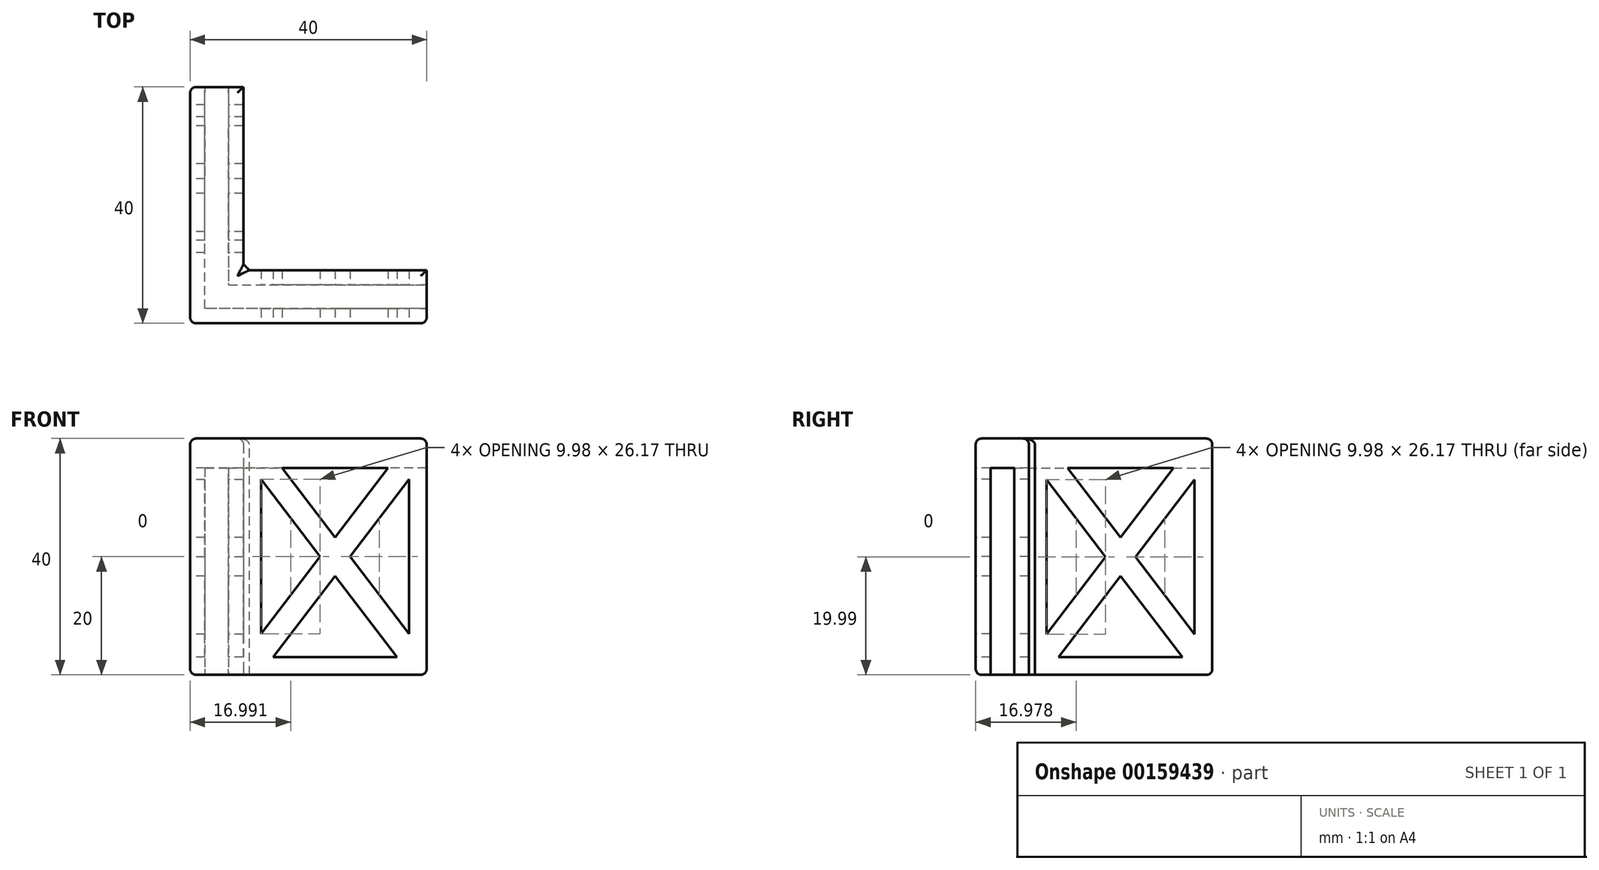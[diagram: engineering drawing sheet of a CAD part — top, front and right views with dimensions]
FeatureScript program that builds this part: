
annotation { "Feature Type Name" : "Feature", "Feature Type Description" : "" }
export const myFeature = defineFeature(function(context is Context, id is Id, definition is map)
    precondition{}
    {
        {
            var Q0;
            Q0=qCreatedBy(makeId("Top.planeOp"),FACE);
            var sketch = newSketch(context, id + "F0", { "sketchPlane" : qUnion([Q0])});
            skLineSegment(sketch, "E0.bottom", {"start": v(-0.94, -7.53) * mm, "end": v(39.06, -7.53) * mm});
            skLineSegment(sketch, "E0.top", {"start": v(-0.94, -47.53) * mm, "end": v(39.06, -47.53) * mm});
            skLineSegment(sketch, "E0.left", {"start": v(-0.94, -7.53) * mm, "end": v(-0.94, -47.53) * mm});
            skLineSegment(sketch, "E0.right", {"start": v(39.06, -7.53) * mm, "end": v(39.06, -47.53) * mm});
            skSolve(sketch);
        }
        {
            var Q0;
            Q0=makeQuery(id+"F0.imprint","IMPRINT",FACE,{"disambiguationData":[TD([[makeQuery(id+"F0.imprint","IMPRINT",EDGE,{"derivedFrom":sQuery(id+"F0.wireOp",EDGE,"E0.bottom")}),-1.0]])]});
            extrude(context, id + "F1", {"entities" : qUnion([Q0]), "depth" : 40 * mm});
        }
        {
            var Q0;
            Q0=makeQuery(id+"F1.opExtrude","CAP_FACE",FACE,{"disambiguationData":[OSD([sQuery(id+"F0.wireOp",EDGE,"E0.bottom"),sQuery(id+"F0.wireOp",EDGE,"E0.top"),sQuery(id+"F0.wireOp",EDGE,"E0.left"),sQuery(id+"F0.wireOp",EDGE,"E0.right")])],"isStart":true});
            var sketch = newSketch(context, id + "F2", { "sketchPlane" : qUnion([Q0])});
            skLineSegment(sketch, "E1", {"start": v(39.06, 45.03) * mm, "end": v(1.56, 45.03) * mm});
            skLineSegment(sketch, "E2", {"start": v(1.56, 45.03) * mm, "end": v(1.56, 7.53) * mm});
            skLineSegment(sketch, "E3", {"start": v(5.56, 7.53) * mm, "end": v(5.56, 41.03) * mm});
            skLineSegment(sketch, "E4", {"start": v(5.56, 41.03) * mm, "end": v(39.06, 41.03) * mm});
            skLineSegment(sketch, "E5", {"start": v(39.06, 38.53) * mm, "end": v(8.06, 38.53) * mm});
            skLineSegment(sketch, "E6", {"start": v(8.06, 38.53) * mm, "end": v(8.06, 7.53) * mm});
            skSolve(sketch);
        }
        {
            var Q0;
            {var subQ3=sQuery(id+"F2.wireOp",EDGE,"E1");Q0=makeQuery(id+"F2.imprint","IMPRINT",FACE,{"disambiguationData":[TD([[makeQuery(id+"F2.imprint","IMPRINT",EDGE,{"derivedFrom":subQ3}),1.0]])]});}
            extrude(context, id + "F3", {"entities" : qUnion([Q0]), "operationType" : NewBodyOperationType.REMOVE, "oppositeDirection" : true, "depth" : 35 * mm});
        }
        {
            var Q0;
            {var subQ0=sQuery(id+"F2.wireOp",EDGE,"E5");Q0=makeQuery(id+"F2.imprint","IMPRINT",FACE,{"disambiguationData":[TD([[makeQuery(id+"F2.imprint","IMPRINT",EDGE,{"derivedFrom":subQ0}),1.0]])]});}
            extrude(context, id + "F4", {"entities" : qUnion([Q0]), "operationType" : NewBodyOperationType.REMOVE, "endBound" : BoundingType.THROUGH_ALL, "oppositeDirection" : true, "depth" : 25 * mm});
        }
        {
            var Q0;
            Q0=makeQuery(id+"F4.boolean.opBoolean","COPY",EDGE,{"derivedFrom":makeQuery(id+"F4.opExtrude","SWEPT_EDGE",EDGE,{"disambiguationData":[OSD([sQuery(id+"F0.wireOp",EDGE,"E0.bottom"),sQuery(id+"F2.wireOp",EDGE,"E6")])]})});
            var Q1;
            Q1=makeQuery(id+"F1.opExtrude","SWEPT_EDGE",EDGE,{"disambiguationData":[OSD([sQuery(id+"F0.wireOp",EDGE,"E0.bottom"),sQuery(id+"F0.wireOp",EDGE,"E0.left")])]});
            var Q2;
            Q2=makeQuery(id+"F1.opExtrude","SWEPT_EDGE",EDGE,{"disambiguationData":[OSD([sQuery(id+"F0.wireOp",EDGE,"E0.top"),sQuery(id+"F0.wireOp",EDGE,"E0.left")])]});
            var Q3;
            Q3=makeQuery(id+"F4.boolean.opBoolean","COPY",EDGE,{"derivedFrom":makeQuery(id+"F4.opExtrude","SWEPT_EDGE",EDGE,{"disambiguationData":[OSD([sQuery(id+"F0.wireOp",EDGE,"E0.right"),sQuery(id+"F2.wireOp",EDGE,"E5")])]})});
            var Q4;
            Q4=makeQuery(id+"F1.opExtrude","SWEPT_EDGE",EDGE,{"disambiguationData":[OSD([sQuery(id+"F0.wireOp",EDGE,"E0.top"),sQuery(id+"F0.wireOp",EDGE,"E0.right")])]});
            var Q5;
            Q5=makeQuery(id+"F1.opExtrude","CAP_EDGE",EDGE,{"disambiguationData":[OSD([sQuery(id+"F0.wireOp",EDGE,"E0.right")])],"isStart":false});
            var Q6;
            Q6=makeQuery(id+"F1.opExtrude","CAP_EDGE",EDGE,{"disambiguationData":[OSD([sQuery(id+"F0.wireOp",EDGE,"E0.top")])],"isStart":false});
            var Q7;
            Q7=makeQuery(id+"F4.boolean.opBoolean","INTERSECT",EDGE,{"derivedFrom":[makeQuery(id+"F1.opExtrude","CAP_FACE",FACE,{"disambiguationData":[OSD([sQuery(id+"F0.wireOp",EDGE,"E0.bottom"),sQuery(id+"F0.wireOp",EDGE,"E0.top"),sQuery(id+"F0.wireOp",EDGE,"E0.left"),sQuery(id+"F0.wireOp",EDGE,"E0.right")])],"isStart":false}),makeQuery(id+"F4.opExtrude","SWEPT_FACE",FACE,{"disambiguationData":[OSD([sQuery(id+"F2.wireOp",EDGE,"E5")])]})]});
            var Q8;
            Q8=makeQuery(id+"F4.boolean.opBoolean","INTERSECT",EDGE,{"derivedFrom":[makeQuery(id+"F1.opExtrude","CAP_FACE",FACE,{"disambiguationData":[OSD([sQuery(id+"F0.wireOp",EDGE,"E0.bottom"),sQuery(id+"F0.wireOp",EDGE,"E0.top"),sQuery(id+"F0.wireOp",EDGE,"E0.left"),sQuery(id+"F0.wireOp",EDGE,"E0.right")])],"isStart":false}),makeQuery(id+"F4.opExtrude","SWEPT_FACE",FACE,{"disambiguationData":[OSD([sQuery(id+"F2.wireOp",EDGE,"E6")])]})]});
            var Q9;
            Q9=makeQuery(id+"F1.opExtrude","CAP_EDGE",EDGE,{"disambiguationData":[OSD([sQuery(id+"F0.wireOp",EDGE,"E0.bottom")])],"isStart":false});
            var Q10;
            Q10=makeQuery(id+"F1.opExtrude","CAP_EDGE",EDGE,{"disambiguationData":[OSD([sQuery(id+"F0.wireOp",EDGE,"E0.left")])],"isStart":false});
            var Q11;
            Q11=makeQuery(id+"F1.opExtrude","CAP_EDGE",EDGE,{"disambiguationData":[OSD([sQuery(id+"F0.wireOp",EDGE,"E0.top")])],"isStart":true});
            var Q12;
            Q12=makeQuery(id+"F4.boolean.opBoolean","COPY",EDGE,{"derivedFrom":makeQuery(id+"F4.opExtrude","CAP_EDGE",EDGE,{"disambiguationData":[OSD([sQuery(id+"F2.wireOp",EDGE,"E5")])],"isStart":true})});
            var Q13;
            Q13=makeQuery(id+"F4.boolean.opBoolean","COPY",EDGE,{"derivedFrom":makeQuery(id+"F4.opExtrude","CAP_EDGE",EDGE,{"disambiguationData":[OSD([sQuery(id+"F2.wireOp",EDGE,"E6")])],"isStart":true})});
            var Q14;
            Q14=makeQuery(id+"F1.opExtrude","CAP_EDGE",EDGE,{"disambiguationData":[OSD([sQuery(id+"F0.wireOp",EDGE,"E0.left")])],"isStart":true});
            var Q15;
            {var subQ0=sQuery(id+"F0.wireOp",EDGE,"E0.right");var subQ1=sQuery(id+"F0.wireOp",EDGE,"E0.top");Q15=makeQuery(id+"F3.boolean.opBoolean","SPLIT",EDGE,{"disambiguationData":[TD([makeQuery(id+"F1.opExtrude","SWEPT_FACE",FACE,{"disambiguationData":[OSD([subQ1])]})])],"derivedFrom":makeQuery(id+"F1.opExtrude","CAP_EDGE",EDGE,{"disambiguationData":[OSD([subQ0])],"isStart":true})});}
            var Q16;
            {var subQ0=sQuery(id+"F0.wireOp",EDGE,"E0.bottom");var subQ1=sQuery(id+"F0.wireOp",EDGE,"E0.right");Q16=makeQuery(id+"F3.boolean.opBoolean","SPLIT",EDGE,{"disambiguationData":[TD([makeQuery(id+"F1.opExtrude","SWEPT_FACE",FACE,{"disambiguationData":[OSD([subQ0])]})])],"derivedFrom":makeQuery(id+"F1.opExtrude","CAP_EDGE",EDGE,{"disambiguationData":[OSD([subQ1])],"isStart":true})});}
            var Q17;
            {var subQ0=sQuery(id+"F0.wireOp",EDGE,"E0.bottom");var subQ1=sQuery(id+"F0.wireOp",EDGE,"E0.right");Q17=makeQuery(id+"F3.boolean.opBoolean","SPLIT",EDGE,{"disambiguationData":[TD([makeQuery(id+"F1.opExtrude","SWEPT_FACE",FACE,{"disambiguationData":[OSD([subQ1])]})])],"derivedFrom":makeQuery(id+"F1.opExtrude","CAP_EDGE",EDGE,{"disambiguationData":[OSD([subQ0])],"isStart":true})});}
            var Q18;
            {var subQ0=sQuery(id+"F0.wireOp",EDGE,"E0.bottom");var subQ1=sQuery(id+"F0.wireOp",EDGE,"E0.left");Q18=makeQuery(id+"F3.boolean.opBoolean","SPLIT",EDGE,{"disambiguationData":[TD([makeQuery(id+"F1.opExtrude","SWEPT_FACE",FACE,{"disambiguationData":[OSD([subQ1])]})])],"derivedFrom":makeQuery(id+"F1.opExtrude","CAP_EDGE",EDGE,{"disambiguationData":[OSD([subQ0])],"isStart":true})});}
            fillet(context, id + "F5", {"entities" : qUnion([Q0, Q1, Q2, Q3, Q4, Q5, Q6, Q7, Q8, Q9, Q10, Q11, Q12, Q13, Q14, Q15, Q16, Q17, Q18]), "radius" : 1 * mm, "tangentPropagation" : true, "allowEdgeOverflow" : false});
        }
        {
            var Q0;
            Q0=makeQuery(id+"F4.boolean.opBoolean","COPY",EDGE,{"derivedFrom":makeQuery(id+"F4.opExtrude","SWEPT_EDGE",EDGE,{"disambiguationData":[OSD([sQuery(id+"F2.wireOp",EDGE,"E5"),sQuery(id+"F2.wireOp",EDGE,"E6")])]})});
            chamfer(context, id + "F6", {"entities" : qUnion([Q0]), "width" : 1 * mm, "tangentPropagation" : true});
        }
        {
            var Q0;
            Q0=makeQuery(id+"F1.opExtrude","SWEPT_FACE",FACE,{"disambiguationData":[OSD([sQuery(id+"F0.wireOp",EDGE,"E0.top")])]});
            var sketch = newSketch(context, id + "F7", { "sketchPlane" : qUnion([Q0])});
            skLineSegment(sketch, "E7", {"start": v(9.06, 39) * mm, "end": v(9.06, 1) * mm});
            skLineSegment(sketch, "E8", {"start": v(11.57, 39) * mm, "end": v(38.06, 4.3) * mm});
            skLineSegment(sketch, "E9", {"start": v(9.06, 35.7) * mm, "end": v(35.54, 1) * mm});
            skLineSegment(sketch, "E10", {"start": v(35.54, 1) * mm, "end": v(35.3, 0.76) * mm});
            skLineSegment(sketch, "E11", {"start": v(35.54, 39) * mm, "end": v(9.06, 4.3) * mm});
            skLineSegment(sketch, "E12", {"start": v(11.57, 1) * mm, "end": v(38.06, 35.7) * mm});
            skLineSegment(sketch, "E13", {"start": v(14.63, 35) * mm, "end": v(32.5, 35) * mm});
            skLineSegment(sketch, "E14", {"start": v(36.06, 33.08) * mm, "end": v(36.06, 6.92) * mm});
            skLineSegment(sketch, "E15", {"start": v(11.06, 33.08) * mm, "end": v(11.06, 6.92) * mm});
            skLineSegment(sketch, "E16", {"start": v(13.1, 3) * mm, "end": v(34.02, 3) * mm});
            skSolve(sketch);
        }
        {
            var Q0;
            {var subQ0=sQuery(id+"F7.wireOp",EDGE,"E13");Q0=makeQuery(id+"F7.imprint","IMPRINT",FACE,{"disambiguationData":[TD([[makeQuery(id+"F7.imprint","IMPRINT",EDGE,{"derivedFrom":subQ0}),-1.0]])]});}
            var Q1;
            {var subQ0=sQuery(id+"F7.wireOp",EDGE,"E15");Q1=makeQuery(id+"F7.imprint","IMPRINT",FACE,{"disambiguationData":[TD([[makeQuery(id+"F7.imprint","IMPRINT",EDGE,{"derivedFrom":subQ0}),1.0]])]});}
            var Q2;
            {var subQ0=sQuery(id+"F7.wireOp",EDGE,"E16");Q2=makeQuery(id+"F7.imprint","IMPRINT",FACE,{"disambiguationData":[TD([[makeQuery(id+"F7.imprint","IMPRINT",EDGE,{"derivedFrom":subQ0}),1.0]])]});}
            var Q3;
            {var subQ0=sQuery(id+"F7.wireOp",EDGE,"E14");Q3=makeQuery(id+"F7.imprint","IMPRINT",FACE,{"disambiguationData":[TD([[makeQuery(id+"F7.imprint","IMPRINT",EDGE,{"derivedFrom":subQ0}),-1.0]])]});}
            extrude(context, id + "F8", {"entities" : qUnion([Q0, Q1, Q2, Q3]), "operationType" : NewBodyOperationType.REMOVE, "endBound" : BoundingType.THROUGH_ALL, "oppositeDirection" : true, "depth" : 25 * mm});
        }
        {
            var Q0;
            Q0=makeQuery(id+"F1.opExtrude","SWEPT_FACE",FACE,{"disambiguationData":[OSD([sQuery(id+"F0.wireOp",EDGE,"E0.left")])]});
            var sketch = newSketch(context, id + "F9", { "sketchPlane" : qUnion([Q0])});
            skLineSegment(sketch, "E17", {"start": v(37.54, 39) * mm, "end": v(37.54, 1) * mm});
            skLineSegment(sketch, "E18.MirrorCS", {"start": v(35.54, 33.07) * mm, "end": v(35.54, 6.9) * mm});
            skLineSegment(sketch, "E19.MirrorCS", {"start": v(37.54, 35.7) * mm, "end": v(11.06, 1) * mm});
            skLineSegment(sketch, "E20.MirrorCS", {"start": v(35.03, 39) * mm, "end": v(8.54, 4.29) * mm});
            skLineSegment(sketch, "E21.MirrorCS", {"start": v(31.98, 35) * mm, "end": v(14.1, 35) * mm});
            skLineSegment(sketch, "E22.MirrorCS", {"start": v(11.06, 39) * mm, "end": v(37.54, 4.29) * mm});
            skLineSegment(sketch, "E23.MirrorCS", {"start": v(35.03, 1) * mm, "end": v(8.54, 35.7) * mm});
            skLineSegment(sketch, "E24.MirrorCS", {"start": v(10.54, 33.07) * mm, "end": v(10.54, 6.9) * mm});
            skLineSegment(sketch, "E25.MirrorCS", {"start": v(33.5, 3) * mm, "end": v(12.59, 3) * mm});
            skSolve(sketch);
        }
        {
            var Q0;
            {var subQ0=sQuery(id+"F9.wireOp",EDGE,"E21.MirrorCS");Q0=makeQuery(id+"F9.imprint","IMPRINT",FACE,{"disambiguationData":[TD([[makeQuery(id+"F9.imprint","IMPRINT",EDGE,{"derivedFrom":subQ0}),1.0]])]});}
            var Q1;
            {var subQ0=sQuery(id+"F9.wireOp",EDGE,"E24.MirrorCS");Q1=makeQuery(id+"F9.imprint","IMPRINT",FACE,{"disambiguationData":[TD([[makeQuery(id+"F9.imprint","IMPRINT",EDGE,{"derivedFrom":subQ0}),1.0]])]});}
            var Q2;
            {var subQ0=sQuery(id+"F9.wireOp",EDGE,"E25.MirrorCS");Q2=makeQuery(id+"F9.imprint","IMPRINT",FACE,{"disambiguationData":[TD([[makeQuery(id+"F9.imprint","IMPRINT",EDGE,{"derivedFrom":subQ0}),-1.0]])]});}
            var Q3;
            {var subQ0=sQuery(id+"F9.wireOp",EDGE,"E18.MirrorCS");Q3=makeQuery(id+"F9.imprint","IMPRINT",FACE,{"disambiguationData":[TD([[makeQuery(id+"F9.imprint","IMPRINT",EDGE,{"derivedFrom":subQ0}),-1.0]])]});}
            extrude(context, id + "F10", {"entities" : qUnion([Q0, Q1, Q2, Q3]), "operationType" : NewBodyOperationType.REMOVE, "endBound" : BoundingType.THROUGH_ALL, "oppositeDirection" : true, "depth" : 25 * mm});
        }
    });
